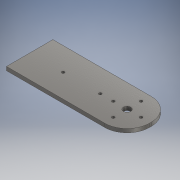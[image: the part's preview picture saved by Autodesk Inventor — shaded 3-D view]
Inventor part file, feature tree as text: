
AUTODESK INVENTOR PART (.ipt)
format: ipt  version: 2018 (Build 220112000, 112)  size: 125,440 bytes
history: native  units: mm
features: fillet x2, other x1, extrude x1, sketch x1
ambient origin geometry x8: Origin, YZ Plane, XZ Plane, XY Plane, X Axis, Y Axis, Z Axis, Center Point
bodies: Body1 (feature_tree)
feature tree (5):
  other  "Sólido1"
  extrude  "Extrusión1"  Depth=25.0mm
  fillet  "Empalme1"  Radius=1.5mm
  fillet  "Empalme2"  Radius=1.5mm
  sketch  "Boceto1"  dims[d0=65.0mm d1=25.0mm d11=1.5mm d12=1.5mm d13=1.5mm d14=4.0mm d15=1.5mm d16=1.5mm d17=1.5mm d18=2.0mm d19=0.0mm d20=12.0mm d21=12.0mm]
